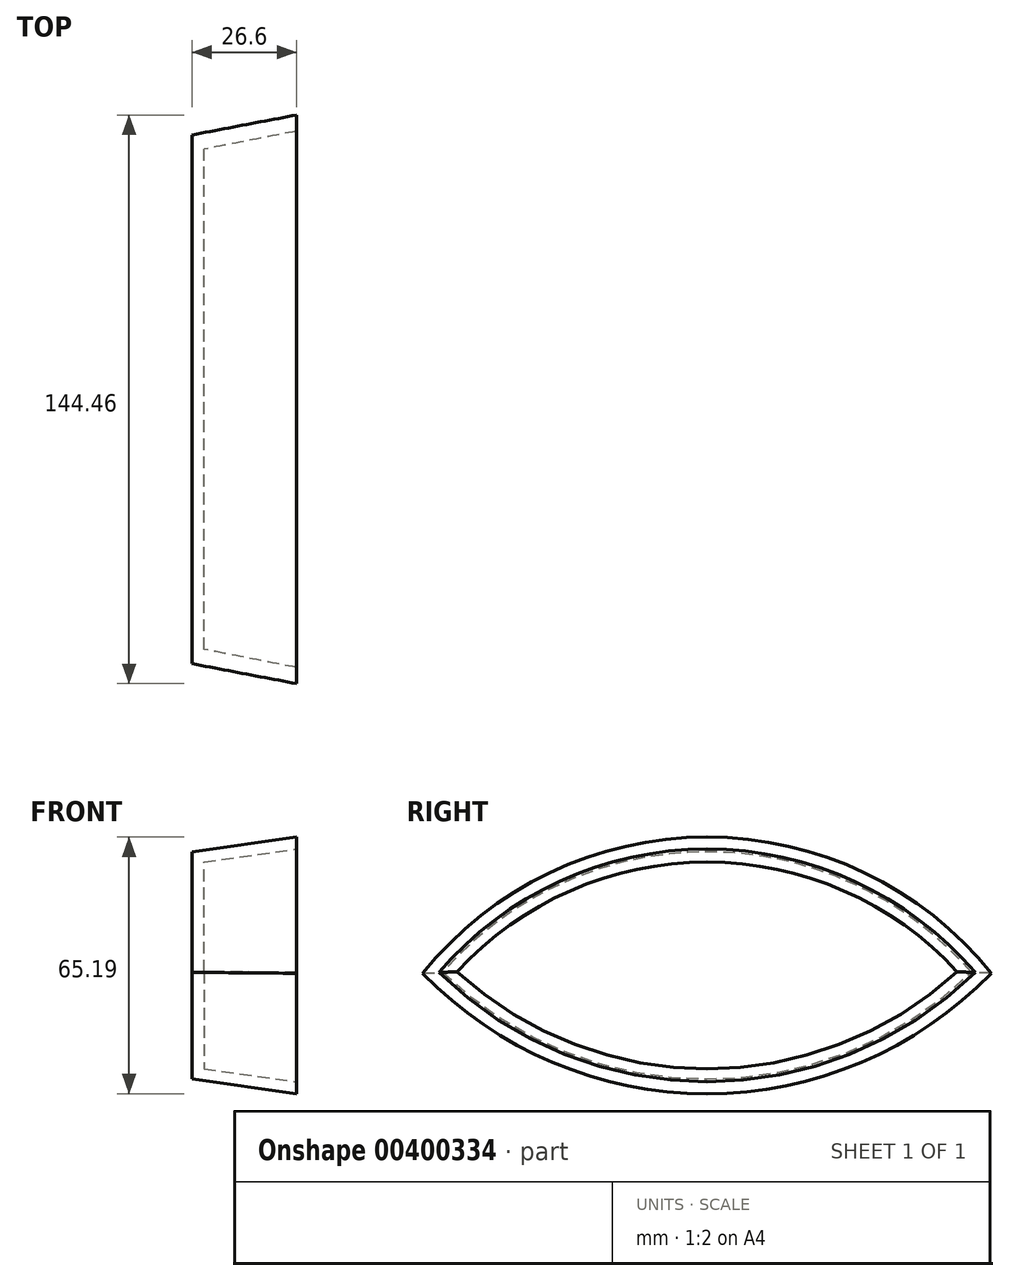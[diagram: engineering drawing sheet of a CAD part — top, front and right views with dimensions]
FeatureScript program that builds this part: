
annotation { "Feature Type Name" : "Feature", "Feature Type Description" : "" }
export const myFeature = defineFeature(function(context is Context, id is Id, definition is map)
    precondition{}
    {
        {
            var Q0;
            Q0=qCreatedBy(makeId("Right.planeOp"),FACE);
            var sketch = newSketch(context, id + "F0", { "sketchPlane" : qUnion([Q0])});
            skArc(sketch, "E0", {"start": v(66.43, 0) * mm, "mid": v(-0.74, 30.63) * mm, "end": v(-67.9, 0) * mm});
            skArc(sketch, "E1", {"start": v(-67.9, 0) * mm, "mid": v(-0.74, -27.09) * mm, "end": v(66.43, 0) * mm});
            skSolve(sketch);
        }
        {
            var Q0;
            Q0=makeQuery(id+"F0.imprint","IMPRINT",FACE,{"disambiguationData":[TD([[makeQuery(id+"F0.imprint","IMPRINT",EDGE,{"derivedFrom":sQuery(id+"F0.wireOp",EDGE,"E0")}),1.0]])]});
            extrude(context, id + "F1", {"entities" : qUnion([Q0]), "depth" : 26.6 * mm, "hasDraft" : true, "draftAngle" : 8 * degree});
        }
        {
            var Q0;
            Q0=makeQuery(id+"F1.opExtrude","CAP_FACE",FACE,{"disambiguationData":[OSD([sQuery(id+"F0.wireOp",EDGE,"E0"),sQuery(id+"F0.wireOp",EDGE,"E1")])],"isStart":false});
            shell(context, id + "F2", {"entities" : qUnion([Q0]), "thickness" : 3 * mm});
        }
    });
